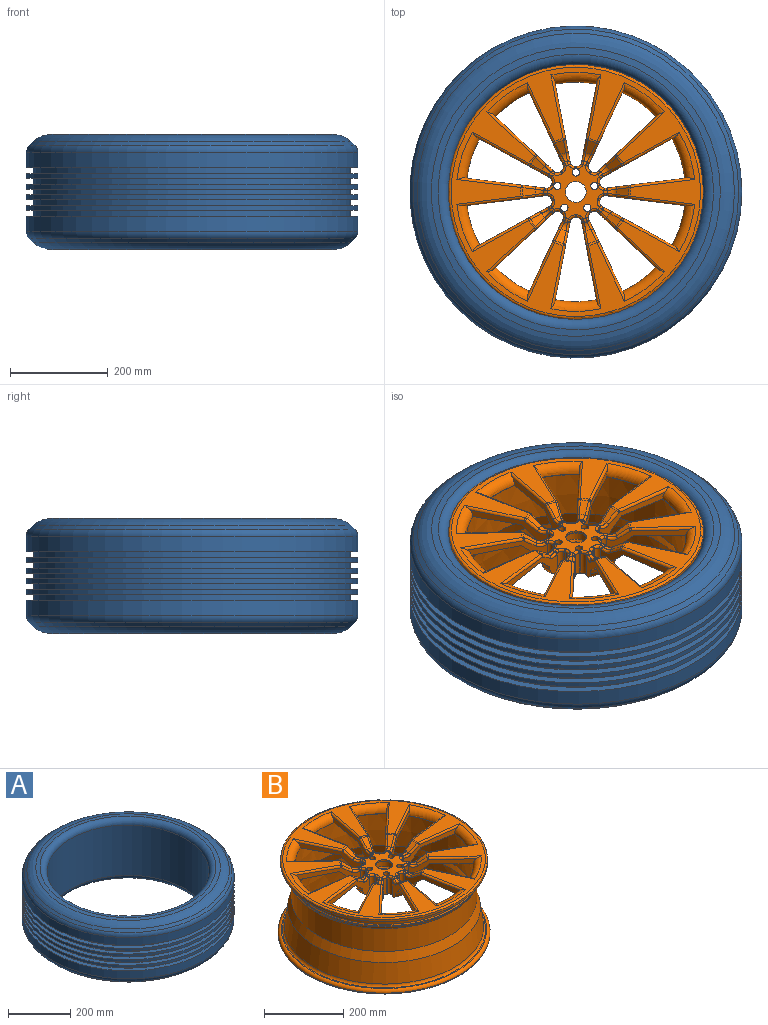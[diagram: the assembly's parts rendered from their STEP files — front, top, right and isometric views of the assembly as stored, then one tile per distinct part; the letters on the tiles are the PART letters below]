
ASSEMBLY  parts=2 mates=1
PART A: 32 faces, bbox 736x736x237.1 mm
  f0: cone r=242.54mm half-angle=84.1deg, axis (0,0,1), area 25407.5mm2, adj f25,f30
  f1: cone r=242.54mm half-angle=84.1deg, axis (0,0,-1), area 25407.5mm2, adj f26,f31
  f2: cylinder r=340mm len=680mm, axis (0,0,1), area 67387.9mm2, adj f3,f28
  f3: plane 680x680mm, normal (0,0,-1), area 31337.4mm2, adj f2,f4
  f4: cylinder r=325mm len=650mm, axis (0,0,1), area 24504.4mm2, adj f3,f5
  f5: plane 680x680mm, normal (0,0,1), area 31337.4mm2, adj f4,f6
  f6: cylinder r=340mm len=680mm, axis (0,0,1), area 20983.1mm2, adj f5,f7
  f7: plane 680x680mm, normal (0,0,-1), area 31337.4mm2, adj f6,f8
  f8: cylinder r=325mm len=650mm, axis (0,0,1), area 24504.4mm2, adj f7,f9
  f9: plane 680x680mm, normal (0,0,1), area 31337.4mm2, adj f8,f10
  f10: cylinder r=340mm len=680mm, axis (0,0,1), area 20983.1mm2, adj f9,f11
  f11: plane 680x680mm, normal (0,0,-1), area 31337.4mm2, adj f10,f12
  f12: cylinder r=325mm len=650mm, axis (0,0,1), area 24504.4mm2, adj f11,f13
  f13: plane 680x680mm, normal (0,0,1), area 31337.4mm2, adj f12,f14
  f14: cylinder r=340mm len=680mm, axis (0,0,1), area 20983.1mm2, adj f13,f15
  f15: plane 680x680mm, normal (0,0,-1), area 31337.4mm2, adj f14,f16
  f16: cylinder r=325mm len=650mm, axis (0,0,1), area 24504.4mm2, adj f15,f17
  f17: plane 680x680mm, normal (0,0,1), area 31337.4mm2, adj f16,f18
  f18: cylinder r=340mm len=680mm, axis (0,0,1), area 20983.1mm2, adj f17,f19
  f19: plane 680x680mm, normal (0,0,-1), area 31337.4mm2, adj f18,f20
  f20: cylinder r=325mm len=650mm, axis (0,0,1), area 24504.4mm2, adj f19,f21
  f21: plane 680x680mm, normal (0,0,1), area 31337.4mm2, adj f20,f22
  f22: cylinder r=340mm len=680mm, axis (0,0,1), area 67387.9mm2, adj f21,f23
  f23: torus R=320mm, axis (0,0,1), area 35064.6mm2, adj f22,f24
  f24: cone r=324.74mm half-angle=47.3deg, axis (0,0,1), area 24808.9mm2, adj f23,f25
  f25: torus R=290.85mm, axis (0,0,1), area 62753mm2, adj f0,f24
  f26: torus R=290.85mm, axis (0,0,1), area 62753mm2, adj f1,f27
  f27: cone r=324.74mm half-angle=47.3deg, axis (0,0,-1), area 24808.9mm2, adj f26,f28
  f28: torus R=320mm, axis (0,0,1), area 35064.6mm2, adj f2,f27
  f29: cylinder r=260mm len=520mm, axis (0,0,-1), area 321947.8mm2, adj f30,f31
  f30: torus R=280mm, axis (0,0,1), area 56379.4mm2, adj f0,f29
  f31: torus R=280mm, axis (0,0,1), area 56379.4mm2, adj f1,f29
PART B: 339 faces, bbox 578.5x578.5x265.2 mm
  f0: cone r=110.52mm half-angle=54.7deg, axis (0,0,1), area 448.4mm2, adj f31,f175,f277,f292
  f1: cone r=110.52mm half-angle=54.7deg, axis (0,0,1), area 448.4mm2, adj f32,f176,f260,f287
  f2: cone r=110.52mm half-angle=54.7deg, axis (0,0,1), area 448.4mm2, adj f33,f174,f304,f309
  f3: cone r=110.52mm half-angle=54.7deg, axis (0,0,1), area 448.4mm2, adj f34,f173,f319,f324
  f4: cone r=110.52mm half-angle=54.7deg, axis (0,0,1), area 448.4mm2, adj f35,f178,f228,f255
  f5: cone r=110.52mm half-angle=54.7deg, axis (0,0,1), area 448.4mm2, adj f36,f177,f245,f272
  f6: cone r=110.52mm half-angle=54.7deg, axis (0,0,1), area 448.4mm2, adj f37,f170,f208,f223
  f7: cone r=110.52mm half-angle=54.7deg, axis (0,0,1), area 448.4mm2, adj f38,f169,f213,f240
  f8: cone r=110.52mm half-angle=54.7deg, axis (0,0,1), area 448.4mm2, adj f39,f172,f181,f336
  f9: plane 114.65x110.6mm, normal (0,0,1), area 5789.6mm2, adj f40,f41,f42,f43,f44,f45,f46,f47
  f10: plane 124.57x122.33mm, normal (0,0,-1), area 7403.8mm2, adj f55,f84,f85,f86,f87,f88,f89,f91
  f11: cone r=82.39mm half-angle=12.4deg, axis (0,0,1), area 217.2mm2, adj f20,f120,f127,f145
  f12: cone r=82.39mm half-angle=12.4deg, axis (0,0,1), area 217.2mm2, adj f21,f123,f128,f146
  f13: cone r=82.39mm half-angle=12.4deg, axis (0,0,1), area 217.2mm2, adj f22,f116,f119,f144
  f14: cone r=82.39mm half-angle=12.4deg, axis (0,0,1), area 217.2mm2, adj f23,f96,f115,f143
  f15: cone r=82.39mm half-angle=12.4deg, axis (0,0,1), area 217.2mm2, adj f24,f108,f111,f148
  f16: cone r=82.39mm half-angle=12.4deg, axis (0,0,1), area 217.2mm2, adj f25,f107,f124,f147
  f17: cone r=82.39mm half-angle=12.4deg, axis (0,0,1), area 217.2mm2, adj f26,f100,f103,f140
  f18: cone r=82.39mm half-angle=12.4deg, axis (0,0,1), area 217.2mm2, adj f27,f99,f112,f139
  f19: cone r=82.39mm half-angle=12.4deg, axis (0,0,1), area 217.2mm2, adj f28,f91,f95,f142
  f20: cone r=88.83mm half-angle=46.7deg, axis (0,0,1), area 999.6mm2, adj f11,f29,f120,f127
  f21: cone r=88.83mm half-angle=46.7deg, axis (0,0,1), area 999.6mm2, adj f12,f29,f123,f128
  f22: cone r=88.83mm half-angle=46.7deg, axis (0,0,1), area 999.6mm2, adj f13,f29,f116,f119
  f23: cone r=88.83mm half-angle=46.7deg, axis (0,0,1), area 999.6mm2, adj f14,f29,f96,f115
  f24: cone r=88.83mm half-angle=46.7deg, axis (0,0,1), area 999.6mm2, adj f15,f29,f108,f111
  f25: cone r=88.83mm half-angle=46.7deg, axis (0,0,1), area 999.6mm2, adj f16,f29,f107,f124
  f26: cone r=88.83mm half-angle=46.7deg, axis (0,0,1), area 999.6mm2, adj f17,f29,f100,f103
  f27: cone r=88.83mm half-angle=46.7deg, axis (0,0,1), area 999.6mm2, adj f18,f29,f99,f112
  f28: cone r=88.83mm half-angle=46.7deg, axis (0,0,1), area 999.6mm2, adj f19,f29,f91,f95
  f29: cone r=117.18mm half-angle=87.7deg, axis (0,0,-1), area 48054.9mm2, adj f20,f21,f22,f23,f24,f25,f26,f27
  f30: plane 510.7x510.7mm, normal (0,0,1), area 62097.7mm2, adj f31,f32,f33,f34,f35,f36,f37,f38
  f31: torus R=112.75mm, axis (0,0,-1), area 76.2mm2, adj f0,f30,f276,f291
  f32: torus R=112.75mm, axis (0,0,-1), area 76.2mm2, adj f1,f30,f259,f288
  f33: torus R=112.75mm, axis (0,0,-1), area 76.2mm2, adj f2,f30,f305,f308
  f34: torus R=112.75mm, axis (0,0,-1), area 76.2mm2, adj f3,f30,f320,f323
  f35: torus R=112.75mm, axis (0,0,-1), area 76.2mm2, adj f4,f30,f227,f256
  f36: torus R=112.75mm, axis (0,0,-1), area 76.2mm2, adj f5,f30,f244,f273
  f37: torus R=112.75mm, axis (0,0,-1), area 76.2mm2, adj f6,f30,f209,f224
  f38: torus R=112.75mm, axis (0,0,-1), area 76.2mm2, adj f7,f30,f212,f241
  f39: torus R=112.75mm, axis (0,0,-1), area 76.2mm2, adj f8,f30,f180,f337
  f40: torus R=57.32mm, axis (0,0,-1), area 47.2mm2, adj f9,f175,f279,f280,f294,f295
  f41: torus R=57.32mm, axis (0,0,-1), area 47.2mm2, adj f9,f176,f262,f263,f284,f285
  f42: torus R=57.32mm, axis (0,0,-1), area 47.2mm2, adj f9,f174,f301,f302,f311,f312
  f43: torus R=57.32mm, axis (0,0,-1), area 47.2mm2, adj f9,f173,f316,f317,f326,f327
  f44: torus R=57.32mm, axis (0,0,-1), area 47.2mm2, adj f9,f178,f230,f231,f252,f253
  f45: torus R=57.32mm, axis (0,0,-1), area 47.2mm2, adj f9,f177,f247,f248,f269,f270
  f46: torus R=57.32mm, axis (0,0,-1), area 47.2mm2, adj f9,f170,f205,f206,f220,f221
  f47: torus R=57.32mm, axis (0,0,-1), area 47.2mm2, adj f9,f169,f215,f216,f237,f238
  f48: torus R=57.32mm, axis (0,0,-1), area 47.2mm2, adj f9,f172,f183,f184,f333,f334
  f49: cone r=110.52mm half-angle=54.7deg, axis (0,0,1), area 448.4mm2, adj f82,f171,f191,f196
  f50: cylinder r=21.19mm len=42.38mm, axis (0,0,1), area 525.7mm2, adj f9,f51
  f51: cone r=21.19mm half-angle=45deg, axis (0,0,-1), area 777.8mm2, adj f50,f52
  f52: cylinder r=24.98mm len=49.97mm, axis (0,0,1), area 2423.2mm2, adj f51,f53
  f53: cone r=24.98mm half-angle=30deg, axis (0,0,1), area 842mm2, adj f52,f54
  f54: cylinder r=22.14mm len=44.28mm, axis (0,0,1), area 1274.6mm2, adj f53,f55
  f55: cone r=22.14mm half-angle=11deg, axis (0,0,-1), area 2600.1mm2, adj f10,f54
  f56: cone r=82.39mm half-angle=12.4deg, axis (0,0,1), area 217.2mm2, adj f57,f92,f104,f141
  f57: cone r=88.83mm half-angle=46.7deg, axis (0,0,1), area 999.6mm2, adj f29,f56,f92,f104
  f58: cone r=226.38mm half-angle=1.9deg, axis (0,0,-1), area 144580.2mm2, adj f29,f59
  f59: cone r=229.67mm half-angle=18.9deg, axis (0,0,-1), area 43557.3mm2, adj f58,f60
  f60: cone r=239.25mm half-angle=7deg, axis (0,0,-1), area 116332.7mm2, adj f59,f61
  f61: plane 521.17x521.17mm, normal (0,0,-1), area 19297.8mm2, adj f60,f62
  f62: cylinder r=260.58mm len=521.17mm, axis (0,0,1), area 8225.7mm2, adj f61,f63
  f63: plane 528.75x528.75mm, normal (0,0,-1), area 6253.2mm2, adj f62,f64
  f64: torus R=264.37mm, axis (0,0,1), area 7470.9mm2, adj f63,f65
  f65: cylinder r=267.22mm len=534.44mm, axis (0,0,1), area 1591.6mm2, adj f64,f66
  f66: torus R=258.69mm, axis (0,0,1), area 22238.8mm2, adj f65,f67
  f67: plane 517.37x517.37mm, normal (0,0,1), area 4596.8mm2, adj f66,f68
  f68: torus R=262.19mm, axis (0,0,1), area 15593.5mm2, adj f67,f69
  f69: cone r=250.64mm half-angle=7deg, axis (0,0,-1), area 95287.6mm2, adj f68,f70
  f70: cone r=243.14mm half-angle=18.9deg, axis (0,0,-1), area 43899.5mm2, adj f69,f71
  f71: cylinder r=233.65mm len=467.31mm, axis (0,0,1), area 104954.2mm2, adj f70,f72
  f72: cone r=242.12mm half-angle=58.3deg, axis (0,0,1), area 14870.9mm2, adj f71,f73
  f73: cone r=243.73mm half-angle=15.5deg, axis (0,0,1), area 9173mm2, adj f72,f74
  f74: cylinder r=243.73mm len=487.45mm, axis (0,0,1), area 5172.8mm2, adj f73,f75
  f75: cone r=242.03mm half-angle=24.6deg, axis (0,0,-1), area 6200.6mm2, adj f74,f76
  f76: cone r=243.08mm half-angle=5.3deg, axis (0,0,1), area 17274.5mm2, adj f75,f77
  f77: cone r=248.06mm half-angle=41.1deg, axis (0,0,1), area 11685.6mm2, adj f76,f78
  f78: plane 506.45x506.45mm, normal (0,0,-1), area 8130.8mm2, adj f77,f79
  f79: cone r=261.07mm half-angle=59.7deg, axis (0,0,1), area 14682.6mm2, adj f78,f80
  f80: cylinder r=261.07mm len=522.13mm, axis (0,0,1), area 10354.3mm2, adj f79,f81
  f81: torus R=255.35mm, axis (0,0,1), area 10861.1mm2, adj f30,f80
  f82: torus R=112.75mm, axis (0,0,-1), area 76.2mm2, adj f30,f49,f192,f195
  f83: torus R=57.32mm, axis (0,0,-1), area 47.2mm2, adj f9,f171,f188,f189,f198,f199
  f84: cylinder r=7.5mm len=54.33mm, axis (0,0,1), area 2560.3mm2, adj f9,f10,f233,f234,f235
  f85: cylinder r=7.5mm len=54.33mm, axis (0,0,1), area 2560.3mm2, adj f9,f10,f201,f202,f203
  f86: cylinder r=7.5mm len=54.33mm, axis (0,0,1), area 2560.3mm2, adj f9,f10,f329,f330,f331
  f87: cylinder r=7.5mm len=54.33mm, axis (0,0,1), area 2560.3mm2, adj f9,f10,f297,f298,f299
  f88: cylinder r=7.5mm len=54.33mm, axis (0,0,1), area 2560.3mm2, adj f9,f10,f265,f266,f267
  f89: cylinder r=52.18mm len=49.33mm, axis (0,0,1), area 144.8mm2, adj f10,f167,f168,f186
  f90: cylinder r=224.86mm len=84.78mm, axis (0,0,1), area 15.5mm2, adj f29,f91,f92,f138
  f91: plane 167.2x66.92mm, normal (0.98,-0.19,0), area 3020.3mm2, adj f10,f19,f28,f29,f90,f138,f142,f168
  f92: plane 167.2x66.92mm, normal (-0.98,-0.19,0), area 3020.3mm2, adj f10,f29,f56,f57,f90,f138,f141,f167
  f93: cylinder r=52.18mm len=49.34mm, axis (0,0,1), area 144.9mm2, adj f10,f149,f150,f330
  f94: cylinder r=224.86mm len=68.59mm, axis (0,0,1), area 15.5mm2, adj f29,f95,f96,f137
  f95: plane 154.14x72.31mm, normal (-0.91,0.42,0), area 3020.3mm2, adj f10,f19,f28,f29,f94,f137,f142,f150
  f96: plane 124.25x116.4mm, normal (0.68,-0.73,0), area 3020.3mm2, adj f10,f14,f23,f29,f94,f137,f143,f149
  f97: cylinder r=52.18mm len=49.33mm, axis (0,0,1), area 144.8mm2, adj f10,f163,f164,f218
  f98: cylinder r=224.86mm len=80.63mm, axis (0,0,1), area 15.5mm2, adj f29,f99,f100,f136
  f99: plane 168.94x66.92mm, normal (-0.12,-0.99,0), area 3020.3mm2, adj f10,f18,f27,f29,f98,f136,f139,f164
  f100: plane 149.1x82.19mm, normal (0.48,0.88,0), area 3020.3mm2, adj f10,f17,f26,f29,f98,f136,f140,f163
  f101: cylinder r=52.18mm len=49.34mm, axis (0,0,1), area 144.9mm2, adj f10,f165,f166,f202
  f102: cylinder r=224.86mm len=68.59mm, axis (0,0,1), area 15.5mm2, adj f29,f103,f104,f135
  f103: plane 124.25x116.4mm, normal (-0.68,-0.73,0), area 3020.3mm2, adj f10,f17,f26,f29,f102,f135,f140,f165
  f104: plane 154.14x72.31mm, normal (0.91,0.42,0), area 3020.3mm2, adj f10,f29,f56,f57,f102,f135,f141,f166
  f105: cylinder r=52.18mm len=49.33mm, axis (0,0,1), area 144.8mm2, adj f10,f159,f160,f250
  f106: cylinder r=224.86mm len=68.59mm, axis (0,0,1), area 15.5mm2, adj f29,f107,f108,f134
  f107: plane 154.14x72.31mm, normal (0.91,-0.42,0), area 3020.3mm2, adj f10,f16,f25,f29,f106,f134,f147,f160
  f108: plane 124.25x116.4mm, normal (-0.68,0.73,0), area 3020.3mm2, adj f10,f15,f24,f29,f106,f134,f148,f159
  f109: cylinder r=52.18mm len=49.34mm, axis (0,0,1), area 144.9mm2, adj f10,f161,f162,f234
  f110: cylinder r=224.86mm len=80.63mm, axis (0,0,1), area 15.5mm2, adj f29,f111,f112,f133
  f111: plane 149.1x82.19mm, normal (0.48,-0.88,0), area 3020.3mm2, adj f10,f15,f24,f29,f110,f133,f148,f162
  f112: plane 168.94x66.92mm, normal (-0.12,0.99,0), area 3020.3mm2, adj f10,f18,f27,f29,f110,f133,f139,f161
  f113: cylinder r=52.18mm len=49.33mm, axis (0,0,1), area 144.8mm2, adj f10,f151,f152,f314
  f114: cylinder r=224.86mm len=80.63mm, axis (0,0,1), area 15.5mm2, adj f29,f115,f116,f132
  f115: plane 149.1x82.19mm, normal (-0.48,0.88,0), area 3020.3mm2, adj f10,f14,f23,f29,f114,f132,f143,f152
  f116: plane 168.94x66.92mm, normal (0.12,-0.99,0), area 3020.3mm2, adj f10,f13,f22,f29,f114,f132,f144,f151
  f117: cylinder r=52.18mm len=49.34mm, axis (0,0,1), area 144.9mm2, adj f10,f153,f154,f298
  f118: cylinder r=224.86mm len=80.63mm, axis (0,0,1), area 15.5mm2, adj f29,f119,f120,f131
  f119: plane 168.94x66.92mm, normal (0.12,0.99,0), area 3020.3mm2, adj f10,f13,f22,f29,f118,f131,f144,f154
  f120: plane 149.1x82.19mm, normal (-0.48,-0.88,0), area 3020.3mm2, adj f10,f11,f20,f29,f118,f131,f145,f153
  f121: cylinder r=52.18mm len=49.34mm, axis (0,0,1), area 144.9mm2, adj f10,f157,f158,f266
  f122: cylinder r=224.86mm len=84.78mm, axis (0,0,1), area 15.5mm2, adj f29,f123,f124,f130
  f123: plane 167.2x66.92mm, normal (0.98,0.19,0), area 3020.3mm2, adj f10,f12,f21,f29,f122,f130,f146,f158
  f124: plane 167.2x66.92mm, normal (-0.98,0.19,0), area 3020.3mm2, adj f10,f16,f25,f29,f122,f130,f147,f157
  f125: cylinder r=52.18mm len=49.33mm, axis (0,0,1), area 144.8mm2, adj f10,f155,f156,f282
  f126: cylinder r=224.86mm len=68.59mm, axis (0,0,1), area 15.5mm2, adj f29,f127,f128,f129
  f127: plane 124.25x116.4mm, normal (0.68,0.73,0), area 3020.3mm2, adj f10,f11,f20,f29,f126,f129,f145,f156
  f128: plane 154.14x72.31mm, normal (-0.91,-0.42,0), area 3020.3mm2, adj f10,f12,f21,f29,f126,f129,f146,f155
  f129: torus R=244.86mm, axis (0,0,-1), area 2821.7mm2, adj f30,f126,f127,f128,f275,f289
  f130: torus R=244.86mm, axis (0,0,-1), area 2821.7mm2, adj f30,f122,f123,f124,f258,f274
  f131: torus R=244.86mm, axis (0,0,-1), area 2821.7mm2, adj f30,f118,f119,f120,f290,f306
  f132: torus R=244.86mm, axis (0,0,-1), area 2821.7mm2, adj f30,f114,f115,f116,f307,f321
  f133: torus R=244.86mm, axis (0,0,-1), area 2821.7mm2, adj f30,f110,f111,f112,f226,f242
  f134: torus R=244.86mm, axis (0,0,-1), area 2821.7mm2, adj f30,f106,f107,f108,f243,f257
  f135: torus R=244.86mm, axis (0,0,-1), area 2821.7mm2, adj f30,f102,f103,f104,f194,f210
  f136: torus R=244.86mm, axis (0,0,-1), area 2821.7mm2, adj f30,f98,f99,f100,f211,f225
  f137: torus R=244.86mm, axis (0,0,-1), area 2821.7mm2, adj f30,f94,f95,f96,f322,f338
  f138: torus R=244.86mm, axis (0,0,-1), area 2821.7mm2, adj f30,f90,f91,f92,f179,f193
  f139: torus R=62.28mm, axis (0,0,1), area 647.4mm2, adj f10,f18,f99,f112
  f140: torus R=62.28mm, axis (0,0,1), area 647.4mm2, adj f10,f17,f100,f103
  f141: torus R=62.28mm, axis (0,0,1), area 647.4mm2, adj f10,f56,f92,f104
  f142: torus R=62.28mm, axis (0,0,1), area 647.4mm2, adj f10,f19,f91,f95
  f143: torus R=62.28mm, axis (0,0,1), area 647.4mm2, adj f10,f14,f96,f115
  f144: torus R=62.28mm, axis (0,0,1), area 647.4mm2, adj f10,f13,f116,f119
  f145: torus R=62.28mm, axis (0,0,1), area 647.4mm2, adj f10,f11,f120,f127
  f146: torus R=62.28mm, axis (0,0,1), area 647.4mm2, adj f10,f12,f123,f128
  f147: torus R=62.28mm, axis (0,0,1), area 647.4mm2, adj f10,f16,f107,f124
  f148: torus R=62.28mm, axis (0,0,1), area 647.4mm2, adj f10,f15,f108,f111
  f149: cylinder r=10mm len=49.34mm, axis (0,0,1), area 693.9mm2, adj f10,f93,f96,f327,f328,f329
  f150: cylinder r=10mm len=49.34mm, axis (0,0,1), area 693.9mm2, adj f10,f93,f95,f331,f332,f333
  f151: cylinder r=10mm len=49.33mm, axis (0,0,1), area 693.9mm2, adj f10,f113,f116,f312,f313
  f152: cylinder r=10mm len=49.33mm, axis (0,0,1), area 693.9mm2, adj f10,f113,f115,f315,f316
  f153: cylinder r=10mm len=49.34mm, axis (0,0,1), area 693.9mm2, adj f10,f117,f120,f295,f296,f297
  f154: cylinder r=10mm len=49.34mm, axis (0,0,1), area 693.9mm2, adj f10,f117,f119,f299,f300,f301
  f155: cylinder r=10mm len=49.33mm, axis (0,0,1), area 693.9mm2, adj f10,f125,f128,f283,f284
  f156: cylinder r=10mm len=49.33mm, axis (0,0,1), area 693.9mm2, adj f10,f125,f127,f280,f281
  f157: cylinder r=10mm len=49.34mm, axis (0,0,1), area 693.9mm2, adj f10,f121,f124,f267,f268,f269
  f158: cylinder r=10mm len=49.34mm, axis (0,0,1), area 693.9mm2, adj f10,f121,f123,f263,f264,f265
  f159: cylinder r=10mm len=49.33mm, axis (0,0,1), area 693.9mm2, adj f10,f105,f108,f251,f252
  f160: cylinder r=10mm len=49.33mm, axis (0,0,1), area 693.9mm2, adj f10,f105,f107,f248,f249
  f161: cylinder r=10mm len=49.34mm, axis (0,0,1), area 693.9mm2, adj f10,f109,f112,f235,f236,f237
  f162: cylinder r=10mm len=49.34mm, axis (0,0,1), area 693.9mm2, adj f10,f109,f111,f231,f232,f233
  f163: cylinder r=10mm len=49.33mm, axis (0,0,1), area 693.9mm2, adj f10,f97,f100,f219,f220
  f164: cylinder r=10mm len=49.33mm, axis (0,0,1), area 693.9mm2, adj f10,f97,f99,f216,f217
  f165: cylinder r=10mm len=49.34mm, axis (0,0,1), area 693.9mm2, adj f10,f101,f103,f203,f204,f205
  f166: cylinder r=10mm len=49.34mm, axis (0,0,1), area 693.9mm2, adj f10,f101,f104,f199,f200,f201
  f167: cylinder r=10mm len=49.33mm, axis (0,0,1), area 693.9mm2, adj f10,f89,f92,f187,f188
  f168: cylinder r=10mm len=49.33mm, axis (0,0,1), area 693.9mm2, adj f10,f89,f91,f184,f185
  f169: torus R=73.87mm, axis (0,0,1), area 148.8mm2, adj f7,f47,f214,f239
  f170: torus R=73.87mm, axis (0,0,1), area 148.8mm2, adj f6,f46,f207,f222
  f171: torus R=73.87mm, axis (0,0,1), area 148.8mm2, adj f49,f83,f190,f197
  f172: torus R=73.87mm, axis (0,0,1), area 148.8mm2, adj f8,f48,f182,f335
  f173: torus R=73.87mm, axis (0,0,1), area 148.8mm2, adj f3,f43,f318,f325
  f174: torus R=73.87mm, axis (0,0,1), area 148.8mm2, adj f2,f42,f303,f310
  f175: torus R=73.87mm, axis (0,0,1), area 148.8mm2, adj f0,f40,f278,f293
  f176: torus R=73.87mm, axis (0,0,1), area 148.8mm2, adj f1,f41,f261,f286
  f177: torus R=73.87mm, axis (0,0,1), area 148.8mm2, adj f5,f45,f246,f271
  f178: torus R=73.87mm, axis (0,0,1), area 148.8mm2, adj f4,f44,f229,f254
  f179: cylinder r=5mm len=130.74mm, axis (0.19,0.98,0), area 981.8mm2, adj f30,f91,f138,f180
  f180: bspline ~7.58x6.22mm, area 24.8mm2, adj f39,f91,f179,f181
  f181: bspline ~93.82x68.91mm, area 247.3mm2, adj f8,f91,f180,f182
  f182: bspline ~25.75x9.04mm, area 159mm2, adj f91,f172,f181,f183
  f183: bspline ~6.16x6.16mm, area 15.4mm2, adj f48,f91,f182,f184
  f184: bspline ~9.88x7.32mm, area 38.7mm2, adj f48,f168,f183,f185
  f185: torus R=15mm, axis (0,0,-1), area 104.3mm2, adj f9,f168,f184,f186
  f186: torus R=47.18mm, axis (0,0,-1), area 22.3mm2, adj f9,f89,f185,f187
  f187: torus R=15mm, axis (0,0,-1), area 104.3mm2, adj f9,f167,f186,f188
  f188: bspline ~9.88x7.32mm, area 38.7mm2, adj f83,f167,f187,f189
  f189: bspline ~6.16x6.16mm, area 15.4mm2, adj f83,f92,f188,f190
  f190: bspline ~25.75x9.04mm, area 159mm2, adj f92,f171,f189,f191
  f191: bspline ~95.04x69.79mm, area 247.3mm2, adj f49,f92,f190,f192
  f192: bspline ~7.58x6.22mm, area 24.8mm2, adj f82,f92,f191,f193
  f193: cylinder r=5mm len=130.74mm, axis (0.19,-0.98,0), area 981.8mm2, adj f30,f92,f138,f192
  f194: cylinder r=5mm len=121.78mm, axis (-0.42,0.91,0), area 981.8mm2, adj f30,f104,f135,f195
  f195: bspline ~8.18x7.26mm, area 24.8mm2, adj f82,f104,f194,f196
  f196: bspline ~49.97x41.12mm, area 247.3mm2, adj f49,f104,f195,f197
  f197: bspline ~23.74x14.54mm, area 159mm2, adj f104,f171,f196,f198
  f198: bspline ~7.33x6.29mm, area 15.4mm2, adj f83,f104,f197,f199
  f199: bspline ~9.43x7.73mm, area 38.7mm2, adj f83,f166,f198,f200
  f200: torus R=15mm, axis (0,0,-1), area 98.8mm2, adj f9,f166,f199,f201
  f201: bspline ~5.08x4.62mm, area 5.2mm2, adj f85,f166,f200,f202
  f202: bspline ~6.42x6.21mm, area 21.8mm2, adj f85,f101,f201,f203
  f203: bspline ~5.15x4.95mm, area 5.2mm2, adj f85,f165,f202,f204
  f204: torus R=15mm, axis (0,0,-1), area 98.8mm2, adj f9,f165,f203,f205
  f205: bspline ~9.65x9.39mm, area 38.7mm2, adj f46,f165,f204,f206
  f206: bspline ~8.28x7.16mm, area 15.4mm2, adj f46,f103,f205,f207
  f207: bspline ~20x19.58mm, area 159mm2, adj f103,f170,f206,f208
  f208: bspline ~71.12x69.79mm, area 247.3mm2, adj f6,f103,f207,f209
  f209: bspline ~8.31x8.17mm, area 24.8mm2, adj f37,f103,f208,f210
  f210: cylinder r=5mm len=99.87mm, axis (0.73,-0.68,0), area 981.8mm2, adj f30,f103,f135,f209
  f211: cylinder r=5mm len=131.77mm, axis (0.99,-0.12,0), area 981.8mm2, adj f30,f99,f136,f212
  f212: bspline ~7.24x5.67mm, area 24.8mm2, adj f38,f99,f211,f213
  f213: bspline ~95x69.79mm, area 247.3mm2, adj f7,f99,f212,f214
  f214: bspline ~26.02x8.81mm, area 159mm2, adj f99,f169,f213,f215
  f215: bspline ~7.03x6.67mm, area 15.4mm2, adj f47,f99,f214,f216
  f216: bspline ~9.48x6.54mm, area 38.7mm2, adj f47,f164,f215,f217
  f217: torus R=15mm, axis (0,0,-1), area 104.3mm2, adj f9,f164,f216,f218
  f218: torus R=47.18mm, axis (0,0,-1), area 22.3mm2, adj f9,f97,f217,f219
  f219: torus R=15mm, axis (0,0,-1), area 104.3mm2, adj f9,f163,f218,f220
  f220: bspline ~9.24x8.4mm, area 38.7mm2, adj f46,f163,f219,f221
  f221: bspline ~7.7x6.85mm, area 15.4mm2, adj f46,f100,f220,f222
  f222: bspline ~22.96x15.26mm, area 159mm2, adj f100,f170,f221,f223
  f223: bspline ~85.17x68.91mm, area 247.3mm2, adj f6,f100,f222,f224
  f224: bspline ~8.28x7.64mm, area 24.8mm2, adj f37,f100,f223,f225
  f225: cylinder r=5mm len=118.16mm, axis (-0.88,0.48,0), area 981.8mm2, adj f30,f100,f136,f224
  f226: cylinder r=5mm len=118.16mm, axis (0.88,0.48,0), area 981.8mm2, adj f30,f111,f133,f227
  f227: bspline ~8.28x7.64mm, area 24.8mm2, adj f35,f111,f226,f228
  f228: bspline ~86.26x69.79mm, area 247.3mm2, adj f4,f111,f227,f229
  f229: bspline ~22.96x15.26mm, area 159mm2, adj f111,f178,f228,f230
  f230: bspline ~7.7x6.85mm, area 15.4mm2, adj f44,f111,f229,f231
  f231: bspline ~10.13x8.92mm, area 38.7mm2, adj f44,f162,f230,f232
  f232: torus R=15mm, axis (0,0,-1), area 98.8mm2, adj f9,f162,f231,f233
  f233: bspline ~5.31x5.15mm, area 5.2mm2, adj f84,f162,f232,f234
  f234: bspline ~5.98x5.45mm, area 21.8mm2, adj f84,f109,f233,f235
  f235: bspline ~5.08x4.88mm, area 5.2mm2, adj f84,f161,f234,f236
  f236: torus R=15mm, axis (0,0,-1), area 98.8mm2, adj f9,f161,f235,f237
  f237: bspline ~8.26x6.5mm, area 38.7mm2, adj f47,f161,f236,f238
  f238: bspline ~7.03x6.67mm, area 15.4mm2, adj f47,f112,f237,f239
  f239: bspline ~26.02x8.81mm, area 159mm2, adj f112,f169,f238,f240
  f240: bspline ~54.77x41.12mm, area 247.3mm2, adj f7,f112,f239,f241
  f241: bspline ~7.24x5.67mm, area 24.8mm2, adj f38,f112,f240,f242
  f242: cylinder r=5mm len=131.77mm, axis (-0.99,-0.12,0), area 981.8mm2, adj f30,f112,f133,f241
  f243: cylinder r=5mm len=121.78mm, axis (0.42,0.91,0), area 981.8mm2, adj f30,f107,f134,f244
  f244: bspline ~8.18x7.26mm, area 24.8mm2, adj f36,f107,f243,f245
  f245: bspline ~51.09x42mm, area 247.3mm2, adj f5,f107,f244,f246
  f246: bspline ~23.74x14.54mm, area 159mm2, adj f107,f177,f245,f247
  f247: bspline ~8.05x6.77mm, area 15.4mm2, adj f45,f107,f246,f248
  f248: bspline ~9.43x7.73mm, area 38.7mm2, adj f45,f160,f247,f249
  f249: torus R=15mm, axis (0,0,-1), area 104.3mm2, adj f9,f160,f248,f250
  f250: torus R=47.18mm, axis (0,0,-1), area 22.3mm2, adj f9,f105,f249,f251
  f251: torus R=15mm, axis (0,0,-1), area 104.3mm2, adj f9,f159,f250,f252
  f252: bspline ~9.65x9.39mm, area 38.7mm2, adj f44,f159,f251,f253
  f253: bspline ~8.28x7.16mm, area 15.4mm2, adj f44,f108,f252,f254
  f254: bspline ~19.02x18.87mm, area 159mm2, adj f108,f178,f253,f255
  f255: bspline ~70.21x68.91mm, area 247.3mm2, adj f4,f108,f254,f256
  f256: bspline ~8.31x8.17mm, area 24.8mm2, adj f35,f108,f255,f257
  f257: cylinder r=5mm len=99.87mm, axis (-0.73,-0.68,0), area 981.8mm2, adj f30,f108,f134,f256
  f258: cylinder r=5mm len=130.74mm, axis (-0.19,0.98,0), area 981.8mm2, adj f30,f123,f130,f259
  f259: bspline ~7.58x6.22mm, area 24.8mm2, adj f32,f123,f258,f260
  f260: bspline ~95.04x69.79mm, area 247.3mm2, adj f1,f123,f259,f261
  f261: bspline ~25.75x9.04mm, area 159mm2, adj f123,f176,f260,f262
  f262: bspline ~6.67x6.47mm, area 15.4mm2, adj f41,f123,f261,f263
  f263: bspline ~9.88x7.32mm, area 38.7mm2, adj f41,f158,f262,f264
  f264: torus R=15mm, axis (0,0,-1), area 98.8mm2, adj f9,f158,f263,f265
  f265: bspline ~5.25x5.24mm, area 5.2mm2, adj f88,f158,f264,f266
  f266: bspline ~5x4.99mm, area 21.8mm2, adj f88,f121,f265,f267
  f267: bspline ~5.25x5.24mm, area 5.2mm2, adj f88,f157,f266,f268
  f268: torus R=15mm, axis (0,0,-1), area 98.8mm2, adj f9,f157,f267,f269
  f269: bspline ~9.88x7.32mm, area 38.7mm2, adj f45,f157,f268,f270
  f270: bspline ~6.24x6.22mm, area 15.4mm2, adj f45,f124,f269,f271
  f271: bspline ~25.75x9.04mm, area 159mm2, adj f124,f177,f270,f272
  f272: bspline ~93.82x68.91mm, area 247.3mm2, adj f5,f124,f271,f273
  f273: bspline ~7.58x6.22mm, area 24.8mm2, adj f36,f124,f272,f274
  f274: cylinder r=5mm len=130.74mm, axis (-0.19,-0.98,0), area 981.8mm2, adj f30,f124,f130,f273
  f275: cylinder r=5mm len=99.87mm, axis (-0.73,0.68,0), area 981.8mm2, adj f30,f127,f129,f276
  f276: bspline ~8.31x8.17mm, area 24.8mm2, adj f31,f127,f275,f277
  f277: bspline ~42.42x42.16mm, area 247.3mm2, adj f0,f127,f276,f278
  f278: bspline ~19.02x18.87mm, area 159mm2, adj f127,f175,f277,f279
  f279: bspline ~8.28x7.16mm, area 15.4mm2, adj f40,f127,f278,f280
  f280: bspline ~9.65x9.39mm, area 38.7mm2, adj f40,f156,f279,f281
  f281: torus R=15mm, axis (0,0,-1), area 104.3mm2, adj f9,f156,f280,f282
  f282: torus R=47.18mm, axis (0,0,-1), area 22.3mm2, adj f9,f125,f281,f283
  f283: torus R=15mm, axis (0,0,-1), area 104.3mm2, adj f9,f155,f282,f284
  f284: bspline ~9.43x7.73mm, area 38.7mm2, adj f41,f155,f283,f285
  f285: bspline ~8.05x6.77mm, area 15.4mm2, adj f41,f128,f284,f286
  f286: bspline ~23.74x14.54mm, area 159mm2, adj f128,f176,f285,f287
  f287: bspline ~85.55x68.91mm, area 247.3mm2, adj f1,f128,f286,f288
  f288: bspline ~8.18x7.26mm, area 24.8mm2, adj f32,f128,f287,f289
  f289: cylinder r=5mm len=121.78mm, axis (0.42,-0.91,0), area 981.8mm2, adj f30,f128,f129,f288
  f290: cylinder r=5mm len=118.16mm, axis (0.88,-0.48,0), area 981.8mm2, adj f30,f120,f131,f291
  f291: bspline ~8.28x7.64mm, area 24.8mm2, adj f31,f120,f290,f292
  f292: bspline ~50.75x41.12mm, area 247.3mm2, adj f0,f120,f291,f293
  f293: bspline ~22.96x15.26mm, area 159mm2, adj f120,f175,f292,f294
  f294: bspline ~7.7x6.85mm, area 15.4mm2, adj f40,f120,f293,f295
  f295: bspline ~9.23x8.2mm, area 38.7mm2, adj f40,f153,f294,f296
  f296: torus R=15mm, axis (0,0,-1), area 98.8mm2, adj f9,f153,f295,f297
  f297: bspline ~5.31x5.15mm, area 5.2mm2, adj f87,f153,f296,f298
  f298: bspline ~5.89x5.45mm, area 21.8mm2, adj f87,f117,f297,f299
  f299: bspline ~5.08x4.88mm, area 5.2mm2, adj f87,f154,f298,f300
  f300: torus R=15mm, axis (0,0,-1), area 98.8mm2, adj f9,f154,f299,f301
  f301: bspline ~9.48x6.54mm, area 38.7mm2, adj f42,f154,f300,f302
  f302: bspline ~7.03x6.67mm, area 15.4mm2, adj f42,f119,f301,f303
  f303: bspline ~26.02x8.81mm, area 159mm2, adj f119,f174,f302,f304
  f304: bspline ~56x42mm, area 247.3mm2, adj f2,f119,f303,f305
  f305: bspline ~7.24x5.67mm, area 24.8mm2, adj f33,f119,f304,f306
  f306: cylinder r=5mm len=131.77mm, axis (-0.99,0.12,0), area 981.8mm2, adj f30,f119,f131,f305
  f307: cylinder r=5mm len=131.77mm, axis (0.99,0.12,0), area 981.8mm2, adj f30,f116,f132,f308
  f308: bspline ~7.24x5.67mm, area 24.8mm2, adj f33,f116,f307,f309
  f309: bspline ~54.77x41.12mm, area 247.3mm2, adj f2,f116,f308,f310
  f310: bspline ~26.02x8.81mm, area 159mm2, adj f116,f174,f309,f311
  f311: bspline ~7.03x6.67mm, area 15.4mm2, adj f42,f116,f310,f312
  f312: bspline ~9.48x6.54mm, area 38.7mm2, adj f42,f151,f311,f313
  f313: torus R=15mm, axis (0,0,-1), area 104.3mm2, adj f9,f151,f312,f314
  f314: torus R=47.18mm, axis (0,0,-1), area 22.3mm2, adj f9,f113,f313,f315
  f315: torus R=15mm, axis (0,0,-1), area 104.3mm2, adj f9,f152,f314,f316
  f316: bspline ~10.13x8.92mm, area 38.7mm2, adj f43,f152,f315,f317
  f317: bspline ~7.7x6.85mm, area 15.4mm2, adj f43,f115,f316,f318
  f318: bspline ~22.96x15.26mm, area 159mm2, adj f115,f173,f317,f319
  f319: bspline ~51.84x42mm, area 247.3mm2, adj f3,f115,f318,f320
  f320: bspline ~8.28x7.64mm, area 24.8mm2, adj f34,f115,f319,f321
  f321: cylinder r=5mm len=118.16mm, axis (-0.88,-0.48,0), area 981.8mm2, adj f30,f115,f132,f320
  f322: cylinder r=5mm len=99.87mm, axis (0.73,0.68,0), area 981.8mm2, adj f30,f96,f137,f323
  f323: bspline ~8.31x8.17mm, area 24.8mm2, adj f34,f96,f322,f324
  f324: bspline ~41.51x41.31mm, area 247.3mm2, adj f3,f96,f323,f325
  f325: bspline ~20x19.58mm, area 159mm2, adj f96,f173,f324,f326
  f326: bspline ~8.28x7.16mm, area 15.4mm2, adj f43,f96,f325,f327
  f327: bspline ~8.86x8.64mm, area 38.7mm2, adj f43,f149,f326,f328
  f328: torus R=15mm, axis (0,0,-1), area 98.8mm2, adj f9,f149,f327,f329
  f329: bspline ~5.15x4.95mm, area 5.2mm2, adj f86,f149,f328,f330
  f330: bspline ~6.36x6.24mm, area 21.8mm2, adj f86,f93,f329,f331
  f331: bspline ~5.18x4.61mm, area 5.2mm2, adj f86,f150,f330,f332
  f332: torus R=15mm, axis (0,0,-1), area 98.8mm2, adj f9,f150,f331,f333
  f333: bspline ~9.43x7.73mm, area 38.7mm2, adj f48,f150,f332,f334
  f334: bspline ~7.13x6.33mm, area 15.4mm2, adj f48,f95,f333,f335
  f335: bspline ~23.74x14.54mm, area 159mm2, adj f95,f172,f334,f336
  f336: bspline ~86.68x69.79mm, area 247.3mm2, adj f8,f95,f335,f337
  f337: bspline ~8.18x7.26mm, area 24.8mm2, adj f39,f95,f336,f338
  f338: cylinder r=5mm len=121.78mm, axis (-0.42,-0.91,0), area 981.8mm2, adj f30,f95,f137,f337
PLACE A t=(0,-233.5,-83)mm
PLACE B t=(0,149.2,-22.41)mm
MATE fastened A.f0 <-> B.f121  axis (0,0,1) through (0,0,29.84)mm
